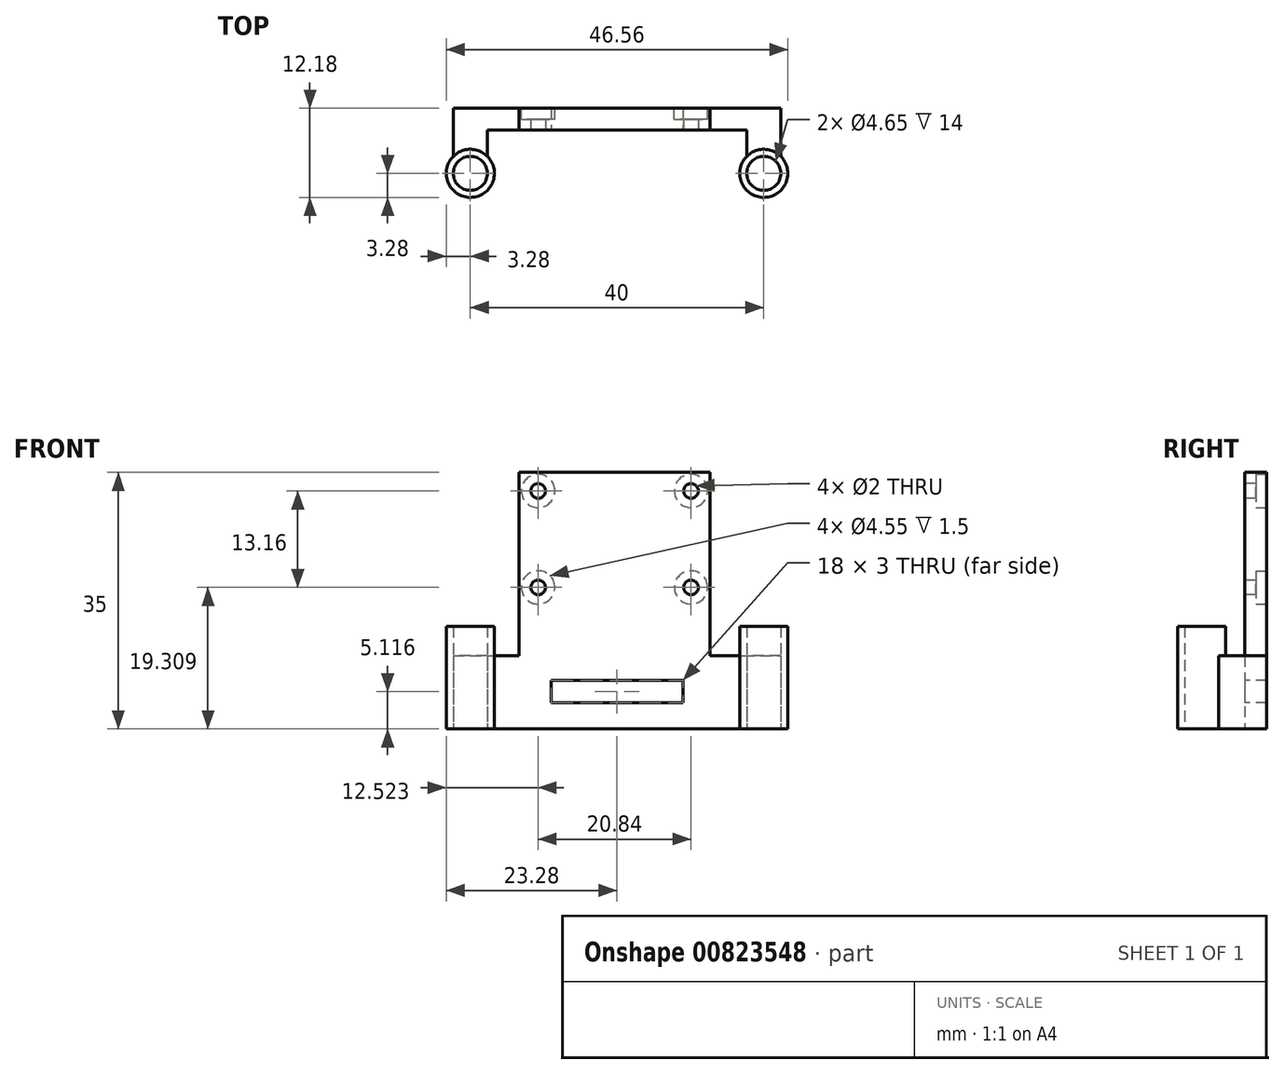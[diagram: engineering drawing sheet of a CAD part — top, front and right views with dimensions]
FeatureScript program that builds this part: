
annotation { "Feature Type Name" : "Feature", "Feature Type Description" : "" }
export const myFeature = defineFeature(function(context is Context, id is Id, definition is map)
    precondition{}
    {
        {
            var Q0;
            Q0=qCreatedBy(makeId("Top.planeOp"),FACE);
            var sketch = newSketch(context, id + "F0", { "sketchPlane" : qUnion([Q0])});
            skCircle(sketch, "E0", {"center": v(-19.76, 0) * mm, "radius": 2.33 * mm});
            skCircle(sketch, "E1", {"center": v(20.24, 0) * mm, "radius": 2.33 * mm});
            skCircle(sketch, "E2", {"center": v(-19.76, 0) * mm, "radius": 3.28 * mm});
            skCircle(sketch, "E3", {"center": v(20.24, 0) * mm, "radius": 3.28 * mm});
            skLineSegment(sketch, "E4", {"start": v(-22.08, 0) * mm, "end": v(-22.08, 8.9) * mm});
            skLineSegment(sketch, "E5", {"start": v(22.57, 0) * mm, "end": v(22.57, 8.9) * mm});
            skLineSegment(sketch, "E6", {"start": v(-19.76, 0) * mm, "end": v(20.24, 0) * mm});
            skLineSegment(sketch, "E7", {"start": v(-22.08, 8.9) * mm, "end": v(22.57, 8.9) * mm});
            skLineSegment(sketch, "E8", {"start": v(-17.43, 0) * mm, "end": v(-17.43, 8.9) * mm});
            skLineSegment(sketch, "E9", {"start": v(17.92, 0) * mm, "end": v(17.92, 8.9) * mm});
            skLineSegment(sketch, "E10", {"start": v(-17.43, 5.9) * mm, "end": v(17.92, 5.9) * mm});
            skSolve(sketch);
        }
        {
            var Q0;
            {var subQ0=sQuery(id+"F0.wireOp",EDGE,"E5");var subQ1=sQuery(id+"F0.wireOp",EDGE,"E1");var subQ2=makeQuery(id+"F0.imprint","INTERSECT",VERTEX,{"derivedFrom":[subQ1,subQ0]});Q0=makeQuery(id+"F0.imprint","IMPRINT",FACE,{"disambiguationData":[TD([[makeQuery(id+"F0.imprint","IMPRINT",EDGE,{"disambiguationData":[TD([[subQ2,1.0]])],"derivedFrom":subQ1}),-1.0]])]});}
            var Q1;
            {var subQ0=sQuery(id+"F0.wireOp",EDGE,"pIkjSwQs-KMYw-8EDy-75vt-u513Ge878Lcs");var subQ1=sQuery(id+"F0.wireOp",EDGE,"E1");var subQ2=makeQuery(id+"F0.imprint","INTERSECT",VERTEX,{"derivedFrom":[subQ1,subQ0]});Q1=makeQuery(id+"F0.imprint","IMPRINT",FACE,{"disambiguationData":[TD([[makeQuery(id+"F0.imprint","IMPRINT",EDGE,{"disambiguationData":[TD([[subQ2,1.0]])],"derivedFrom":subQ1}),-1.0]])]});}
            var Q2;
            {var subQ0=sQuery(id+"F0.wireOp",EDGE,"pIkjSwQs-KMYw-8EDy-75vt-u513Ge878Lcs");var subQ1=sQuery(id+"F0.wireOp",EDGE,"E1");var subQ2=makeQuery(id+"F0.imprint","INTERSECT",VERTEX,{"derivedFrom":[subQ1,subQ0]});Q2=makeQuery(id+"F0.imprint","IMPRINT",FACE,{"disambiguationData":[TD([[makeQuery(id+"F0.imprint","IMPRINT",EDGE,{"disambiguationData":[TD([[subQ2,-1.0]])],"derivedFrom":subQ1}),-1.0]])]});}
            var Q3;
            {var subQ0=sQuery(id+"F0.wireOp",EDGE,"PAsIG5vc-tbBl-nQOd-2SaM-8rldyLJ6n05g");Q3=makeQuery(id+"F0.imprint","IMPRINT",FACE,{"disambiguationData":[TD([[makeQuery(id+"F0.imprint","IMPRINT",EDGE,{"derivedFrom":subQ0}),1.0]])]});}
            var Q4;
            {var subQ0=sQuery(id+"F0.wireOp",EDGE,"z06Rm72J-lbv2-eatK-js9Q-tS6ydxI5LmMU.bottom");Q4=makeQuery(id+"F0.imprint","IMPRINT",FACE,{"disambiguationData":[TD([[makeQuery(id+"F0.imprint","IMPRINT",EDGE,{"derivedFrom":subQ0}),-1.0]])]});}
            var Q5;
            {var subQ0=sQuery(id+"F0.wireOp",EDGE,"zEkp0kuG-he4V-8IWa-PuKW-0BacrWcyJJLC");Q5=makeQuery(id+"F0.imprint","IMPRINT",FACE,{"disambiguationData":[TD([[makeQuery(id+"F0.imprint","IMPRINT",EDGE,{"derivedFrom":subQ0}),-1.0]])]});}
            var Q6;
            {var subQ0=sQuery(id+"F0.wireOp",EDGE,"E4");var subQ1=sQuery(id+"F0.wireOp",EDGE,"E0");var subQ2=makeQuery(id+"F0.imprint","INTERSECT",VERTEX,{"derivedFrom":[subQ1,subQ0]});Q6=makeQuery(id+"F0.imprint","IMPRINT",FACE,{"disambiguationData":[TD([[makeQuery(id+"F0.imprint","IMPRINT",EDGE,{"disambiguationData":[TD([[subQ2,1.0]])],"derivedFrom":subQ1}),-1.0]])]});}
            var Q7;
            {var subQ0=sQuery(id+"F0.wireOp",EDGE,"qbSQwhjJ-SbTz-RbyT-yrnF-y7RLgv9yjtzQ");var subQ1=sQuery(id+"F0.wireOp",EDGE,"E0");var subQ2=makeQuery(id+"F0.imprint","INTERSECT",VERTEX,{"derivedFrom":[subQ1,subQ0]});Q7=makeQuery(id+"F0.imprint","IMPRINT",FACE,{"disambiguationData":[TD([[makeQuery(id+"F0.imprint","IMPRINT",EDGE,{"disambiguationData":[TD([[subQ2,1.0]])],"derivedFrom":subQ1}),-1.0]])]});}
            var Q8;
            {var subQ0=sQuery(id+"F0.wireOp",EDGE,"E4");var subQ1=sQuery(id+"F0.wireOp",EDGE,"E0");var subQ2=makeQuery(id+"F0.imprint","INTERSECT",VERTEX,{"derivedFrom":[subQ1,subQ0]});Q8=makeQuery(id+"F0.imprint","IMPRINT",FACE,{"disambiguationData":[TD([[makeQuery(id+"F0.imprint","IMPRINT",EDGE,{"disambiguationData":[TD([[subQ2,-1.0]])],"derivedFrom":subQ1}),-1.0]])]});}
            var Q9;
            {var subQ0=sQuery(id+"F0.wireOp",EDGE,"E6");var subQ1=sQuery(id+"F0.wireOp",EDGE,"E2");var subQ2=makeQuery(id+"F0.imprint","INTERSECT",VERTEX,{"derivedFrom":[subQ1,subQ0]});Q9=makeQuery(id+"F0.imprint","IMPRINT",FACE,{"disambiguationData":[TD([[makeQuery(id+"F0.imprint","IMPRINT",EDGE,{"disambiguationData":[TD([[subQ2,-1.0]])],"derivedFrom":subQ1}),1.0]])]});}
            var Q10;
            {var subQ1=sQuery(id+"F0.wireOp",EDGE,"E4");var subQ6=sQuery(id+"F0.wireOp",EDGE,"E2");var subQ8=makeQuery(id+"F0.imprint","INTERSECT",VERTEX,{"derivedFrom":[subQ6,subQ1]});Q10=makeQuery(id+"F0.imprint","IMPRINT",FACE,{"disambiguationData":[TD([[makeQuery(id+"F0.imprint","IMPRINT",EDGE,{"disambiguationData":[TD([[subQ8,1.0]])],"derivedFrom":subQ6}),-1.0]])]});}
            var Q11;
            {var subQ5=sQuery(id+"F0.wireOp",EDGE,"E10");Q11=makeQuery(id+"F0.imprint","IMPRINT",FACE,{"disambiguationData":[TD([[makeQuery(id+"F0.imprint","IMPRINT",EDGE,{"derivedFrom":subQ5}),1.0]])]});}
            var Q12;
            {var subQ2=sQuery(id+"F0.wireOp",EDGE,"E3");var subQ5=sQuery(id+"F0.wireOp",EDGE,"E5");var subQ7=makeQuery(id+"F0.imprint","INTERSECT",VERTEX,{"derivedFrom":[subQ2,subQ5]});Q12=makeQuery(id+"F0.imprint","IMPRINT",FACE,{"disambiguationData":[TD([[makeQuery(id+"F0.imprint","IMPRINT",EDGE,{"disambiguationData":[TD([[subQ7,-1.0]])],"derivedFrom":subQ2}),-1.0]])]});}
            var Q13;
            {var subQ0=sQuery(id+"F0.wireOp",EDGE,"E6");var subQ1=sQuery(id+"F0.wireOp",EDGE,"E3");var subQ2=makeQuery(id+"F0.imprint","INTERSECT",VERTEX,{"derivedFrom":[subQ1,subQ0]});Q13=makeQuery(id+"F0.imprint","IMPRINT",FACE,{"disambiguationData":[TD([[makeQuery(id+"F0.imprint","IMPRINT",EDGE,{"disambiguationData":[TD([[subQ2,1.0]])],"derivedFrom":subQ1}),1.0]])]});}
            extrude(context, id + "F1", {"entities" : qUnion([Q0, Q1, Q2, Q3, Q4, Q5, Q6, Q7, Q8, Q9, Q10, Q11, Q12, Q13]), "depth" : 10 * mm, "offsetDistance" : 25 * mm});
        }
        {
            var Q0;
            Q0=makeQuery(id+"F1.opExtrude","CAP_FACE",FACE,{"disambiguationData":[OSD([sQuery(id+"F0.wireOp",EDGE,"E0"),sQuery(id+"F0.wireOp",EDGE,"E1"),sQuery(id+"F0.wireOp",EDGE,"E2"),sQuery(id+"F0.wireOp",EDGE,"E3"),sQuery(id+"F0.wireOp",EDGE,"E4"),sQuery(id+"F0.wireOp",EDGE,"qbSQwhjJ-SbTz-RbyT-yrnF-y7RLgv9yjtzQ"),sQuery(id+"F0.wireOp",EDGE,"zEkp0kuG-he4V-8IWa-PuKW-0BacrWcyJJLC"),sQuery(id+"F0.wireOp",EDGE,"pIkjSwQs-KMYw-8EDy-75vt-u513Ge878Lcs"),sQuery(id+"F0.wireOp",EDGE,"E5"),sQuery(id+"F0.wireOp",EDGE,"PAsIG5vc-tbBl-nQOd-2SaM-8rldyLJ6n05g"),sQuery(id+"F0.wireOp",EDGE,"z06Rm72J-lbv2-eatK-js9Q-tS6ydxI5LmMU.bottom"),sQuery(id+"F0.wireOp",EDGE,"z06Rm72J-lbv2-eatK-js9Q-tS6ydxI5LmMU.top")])],"isStart":false});
            var sketch = newSketch(context, id + "F2", { "sketchPlane" : qUnion([Q0])});
            skPoint(sketch, "E11", {"position": v(0, 12.63) * mm});
            skPoint(sketch, "E12", {"position": v(-0.1, 7.4) * mm});
            skLineSegment(sketch, "E13.bottom", {"start": v(-13.1, 5.9) * mm, "end": v(12.9, 5.9) * mm});
            skLineSegment(sketch, "E13.top", {"start": v(-13.1, 8.9) * mm, "end": v(12.9, 8.9) * mm});
            skLineSegment(sketch, "E13.left", {"start": v(-13.1, 5.9) * mm, "end": v(-13.1, 8.9) * mm});
            skLineSegment(sketch, "E13.right", {"start": v(12.9, 5.9) * mm, "end": v(12.9, 8.9) * mm});
            skSolve(sketch);
        }
        {
            var Q0;
            Q0=makeQuery(id+"F2.imprint","IMPRINT",FACE,{"disambiguationData":[TD([[makeQuery(id+"F2.imprint","IMPRINT",EDGE,{"derivedFrom":sQuery(id+"F2.wireOp",EDGE,"E13.bottom")}),1.0]])]});
            extrude(context, id + "F3", {"entities" : qUnion([Q0]), "operationType" : NewBodyOperationType.ADD, "depth" : 28 * mm, "offsetDistance" : 25 * mm});
        }
        {
            var Q0;
            Q0=makeQuery(id+"F3.boolean.opBoolean","MERGE",FACE,{"derivedFrom":[makeQuery(id+"F1.opExtrude","SWEPT_FACE",FACE,{"disambiguationData":[OSD([sQuery(id+"F0.wireOp",EDGE,"z06Rm72J-lbv2-eatK-js9Q-tS6ydxI5LmMU.top")])]}),makeQuery(id+"F3.opExtrude","SWEPT_FACE",FACE,{"disambiguationData":[OSD([sQuery(id+"F2.wireOp",EDGE,"E13.bottom")])]})]});
            var sketch = newSketch(context, id + "F4", { "sketchPlane" : qUnion([Q0])});
            skCircle(sketch, "E14", {"center": v(-10.52, 35.47) * mm, "radius": 1 * mm});
            skCircle(sketch, "E15", {"center": v(-10.52, 22.3) * mm, "radius": 1 * mm});
            skCircle(sketch, "E16", {"center": v(10.32, 35.47) * mm, "radius": 1 * mm});
            skCircle(sketch, "E17", {"center": v(10.32, 22.3) * mm, "radius": 1 * mm});
            skPoint(sketch, "E18.middle", {"position": v(0, 7.75) * mm});
            skSolve(sketch);
        }
        {
            var Q0;
            Q0=makeQuery(id+"F4.imprint","IMPRINT",FACE,{"disambiguationData":[TD([[makeQuery(id+"F4.imprint","IMPRINT",EDGE,{"derivedFrom":sQuery(id+"F4.wireOp",EDGE,"E14")}),1.0]])]});
            var Q1;
            Q1=makeQuery(id+"F4.imprint","IMPRINT",FACE,{"disambiguationData":[TD([[makeQuery(id+"F4.imprint","IMPRINT",EDGE,{"derivedFrom":sQuery(id+"F4.wireOp",EDGE,"E15")}),1.0]])]});
            var Q2;
            Q2=makeQuery(id+"F4.imprint","IMPRINT",FACE,{"disambiguationData":[TD([[makeQuery(id+"F4.imprint","IMPRINT",EDGE,{"derivedFrom":sQuery(id+"F4.wireOp",EDGE,"E17")}),1.0]])]});
            var Q3;
            Q3=makeQuery(id+"F4.imprint","IMPRINT",FACE,{"disambiguationData":[TD([[makeQuery(id+"F4.imprint","IMPRINT",EDGE,{"derivedFrom":sQuery(id+"F4.wireOp",EDGE,"E16")}),1.0]])]});
            var Q4;
            Q4=makeQuery(id+"F4.imprint","IMPRINT",FACE,{"disambiguationData":[TD([[makeQuery(id+"F4.imprint","IMPRINT",EDGE,{"derivedFrom":sQuery(id+"F4.wireOp",EDGE,"E18.bottom")}),-1.0]])]});
            extrude(context, id + "F5", {"entities" : qUnion([Q0, Q1, Q2, Q3, Q4]), "operationType" : NewBodyOperationType.REMOVE, "endBound" : BoundingType.UP_TO_NEXT, "oppositeDirection" : true, "depth" : 25 * mm, "offsetDistance" : 25 * mm});
        }
        {
            var Q0;
            Q0=makeQuery(id+"F3.boolean.opBoolean","MERGE",FACE,{"derivedFrom":[makeQuery(id+"F1.opExtrude","SWEPT_FACE",FACE,{"disambiguationData":[OSD([sQuery(id+"F0.wireOp",EDGE,"zEkp0kuG-he4V-8IWa-PuKW-0BacrWcyJJLC"),sQuery(id+"F0.wireOp",EDGE,"z06Rm72J-lbv2-eatK-js9Q-tS6ydxI5LmMU.bottom")])]}),makeQuery(id+"F3.opExtrude","SWEPT_FACE",FACE,{"disambiguationData":[OSD([sQuery(id+"F2.wireOp",EDGE,"E13.top")])]})]});
            var sketch = newSketch(context, id + "F6", { "sketchPlane" : qUnion([Q0])});
            skCircle(sketch, "E19", {"center": v(-10.32, 35.47) * mm, "radius": 2.27 * mm});
            skCircle(sketch, "E20", {"center": v(10.52, 35.47) * mm, "radius": 2.27 * mm});
            skCircle(sketch, "E21", {"center": v(-10.32, 22.3) * mm, "radius": 2.27 * mm});
            skCircle(sketch, "E22", {"center": v(10.52, 22.3) * mm, "radius": 2.27 * mm});
            skSolve(sketch);
        }
        {
            var Q0;
            Q0=makeQuery(id+"F6.imprint","IMPRINT",FACE,{"disambiguationData":[TD([[makeQuery(id+"F6.imprint","IMPRINT",EDGE,{"derivedFrom":sQuery(id+"F6.wireOp",EDGE,"E19")}),1.0]])]});
            var Q1;
            Q1=makeQuery(id+"F6.imprint","IMPRINT",FACE,{"disambiguationData":[TD([[makeQuery(id+"F6.imprint","IMPRINT",EDGE,{"derivedFrom":sQuery(id+"F6.wireOp",EDGE,"E21")}),1.0]])]});
            var Q2;
            Q2=makeQuery(id+"F6.imprint","IMPRINT",FACE,{"disambiguationData":[TD([[makeQuery(id+"F6.imprint","IMPRINT",EDGE,{"derivedFrom":sQuery(id+"F6.wireOp",EDGE,"E22")}),1.0]])]});
            var Q3;
            Q3=makeQuery(id+"F6.imprint","IMPRINT",FACE,{"disambiguationData":[TD([[makeQuery(id+"F6.imprint","IMPRINT",EDGE,{"derivedFrom":sQuery(id+"F6.wireOp",EDGE,"E20")}),1.0]])]});
            extrude(context, id + "F7", {"entities" : qUnion([Q0, Q1, Q2, Q3]), "operationType" : NewBodyOperationType.REMOVE, "oppositeDirection" : true, "depth" : 1.5 * mm, "offsetDistance" : 25 * mm});
        }
        {
            var Q0;
            Q0=makeQuery(id+"F1.opExtrude","CAP_FACE",FACE,{"disambiguationData":[OSD([sQuery(id+"F0.wireOp",EDGE,"E0"),sQuery(id+"F0.wireOp",EDGE,"E1"),sQuery(id+"F0.wireOp",EDGE,"E2"),sQuery(id+"F0.wireOp",EDGE,"E3"),sQuery(id+"F0.wireOp",EDGE,"E4"),sQuery(id+"F0.wireOp",EDGE,"E5"),sQuery(id+"F0.wireOp",EDGE,"E7"),sQuery(id+"F0.wireOp",EDGE,"E8"),sQuery(id+"F0.wireOp",EDGE,"E9"),sQuery(id+"F0.wireOp",EDGE,"E10")])],"isStart":true});
            extrude(context, id + "F8", {"entities" : qUnion([Q0]), "operationType" : NewBodyOperationType.REMOVE, "oppositeDirection" : true, "depth" : 3 * mm, "offsetDistance" : 25 * mm});
        }
        {
            var Q0;
            {var subQ0=sQuery(id+"F0.wireOp",EDGE,"E5");var subQ1=sQuery(id+"F0.wireOp",EDGE,"E3");var subQ2=sQuery(id+"F0.wireOp",EDGE,"E7");var subQ3=sQuery(id+"F0.wireOp",EDGE,"E1");var subQ4=sQuery(id+"F0.wireOp",EDGE,"E9");var subQ5=sQuery(id+"F0.wireOp",EDGE,"E10");Q0=makeQuery(id+"F3.boolean.opBoolean","SPLIT",FACE,{"disambiguationData":[TD([makeQuery(id+"F1.opExtrude","SWEPT_FACE",FACE,{"disambiguationData":[OSD([subQ3])]})])],"derivedFrom":makeQuery(id+"F1.opExtrude","CAP_FACE",FACE,{"disambiguationData":[OSD([sQuery(id+"F0.wireOp",EDGE,"E0"),subQ3,sQuery(id+"F0.wireOp",EDGE,"E2"),subQ1,sQuery(id+"F0.wireOp",EDGE,"E4"),subQ0,subQ2,sQuery(id+"F0.wireOp",EDGE,"E8"),subQ4,subQ5])],"isStart":false})});}
            var Q1;
            {var subQ0=sQuery(id+"F0.wireOp",EDGE,"E7");var subQ1=sQuery(id+"F0.wireOp",EDGE,"E4");var subQ2=sQuery(id+"F0.wireOp",EDGE,"E2");var subQ3=sQuery(id+"F0.wireOp",EDGE,"E0");var subQ4=sQuery(id+"F0.wireOp",EDGE,"E10");var subQ5=sQuery(id+"F0.wireOp",EDGE,"E8");Q1=makeQuery(id+"F3.boolean.opBoolean","SPLIT",FACE,{"disambiguationData":[TD([makeQuery(id+"F1.opExtrude","SWEPT_FACE",FACE,{"disambiguationData":[OSD([subQ3])]})])],"derivedFrom":makeQuery(id+"F1.opExtrude","CAP_FACE",FACE,{"disambiguationData":[OSD([subQ3,sQuery(id+"F0.wireOp",EDGE,"E1"),subQ2,sQuery(id+"F0.wireOp",EDGE,"E3"),subQ1,sQuery(id+"F0.wireOp",EDGE,"E5"),subQ0,subQ5,sQuery(id+"F0.wireOp",EDGE,"E9"),subQ4])],"isStart":false})});}
            extrude(context, id + "F9", {"entities" : qUnion([Q0, Q1]), "operationType" : NewBodyOperationType.ADD, "depth" : 3 * mm, "offsetDistance" : 25 * mm});
        }
        {
            var Q0;
            {var subQ0=sQuery(id+"F0.wireOp",EDGE,"E5");var subQ1=sQuery(id+"F0.wireOp",EDGE,"E3");var subQ2=sQuery(id+"F0.wireOp",EDGE,"E7");var subQ3=sQuery(id+"F0.wireOp",EDGE,"E1");var subQ4=sQuery(id+"F0.wireOp",EDGE,"E9");var subQ5=sQuery(id+"F0.wireOp",EDGE,"E10");var subQ6=sQuery(id+"F0.wireOp",EDGE,"E8");var subQ7=sQuery(id+"F0.wireOp",EDGE,"E4");var subQ8=sQuery(id+"F0.wireOp",EDGE,"E2");var subQ9=sQuery(id+"F0.wireOp",EDGE,"E0");Q0=makeQuery(id+"F9.opExtrude","CAP_FACE",FACE,{"disambiguationData":[OSD([subQ9,subQ3,subQ8,subQ1,subQ7,subQ0,subQ2,subQ6,subQ4,subQ5]),TDD([makeQuery(id+"F3.boolean.opBoolean","SPLIT",FACE,{"disambiguationData":[TD([makeQuery(id+"F1.opExtrude","SWEPT_FACE",FACE,{"disambiguationData":[OSD([subQ3])]})])],"derivedFrom":makeQuery(id+"F1.opExtrude","CAP_FACE",FACE,{"disambiguationData":[OSD([subQ9,subQ3,subQ8,subQ1,subQ7,subQ0,subQ2,subQ6,subQ4,subQ5])],"isStart":false})})])],"isStart":false});}
            var sketch = newSketch(context, id + "F10", { "sketchPlane" : qUnion([Q0])});
            skCircle(sketch, "E23", {"center": v(20.24, 0) * mm, "radius": 2.33 * mm});
            skCircle(sketch, "E24", {"center": v(20.24, 0) * mm, "radius": 3.28 * mm});
            skSolve(sketch);
        }
        {
            var Q0;
            {var subQ0=sQuery(id+"F0.wireOp",EDGE,"E7");var subQ1=sQuery(id+"F0.wireOp",EDGE,"E4");var subQ2=sQuery(id+"F0.wireOp",EDGE,"E2");var subQ3=sQuery(id+"F0.wireOp",EDGE,"E0");var subQ4=sQuery(id+"F0.wireOp",EDGE,"E10");var subQ5=sQuery(id+"F0.wireOp",EDGE,"E8");var subQ6=sQuery(id+"F0.wireOp",EDGE,"E9");var subQ7=sQuery(id+"F0.wireOp",EDGE,"E5");var subQ8=sQuery(id+"F0.wireOp",EDGE,"E3");var subQ9=sQuery(id+"F0.wireOp",EDGE,"E1");Q0=makeQuery(id+"F9.opExtrude","CAP_FACE",FACE,{"disambiguationData":[OSD([subQ3,subQ9,subQ2,subQ8,subQ1,subQ7,subQ0,subQ5,subQ6,subQ4]),TDD([makeQuery(id+"F3.boolean.opBoolean","SPLIT",FACE,{"disambiguationData":[TD([makeQuery(id+"F1.opExtrude","SWEPT_FACE",FACE,{"disambiguationData":[OSD([subQ3])]})])],"derivedFrom":makeQuery(id+"F1.opExtrude","CAP_FACE",FACE,{"disambiguationData":[OSD([subQ3,subQ9,subQ2,subQ8,subQ1,subQ7,subQ0,subQ5,subQ6,subQ4])],"isStart":false})})])],"isStart":false});}
            var sketch = newSketch(context, id + "F11", { "sketchPlane" : qUnion([Q0])});
            skCircle(sketch, "E25", {"center": v(-19.76, 0) * mm, "radius": 2.33 * mm});
            skCircle(sketch, "E26", {"center": v(-19.76, 0) * mm, "radius": 3.28 * mm});
            skSolve(sketch);
        }
        {
            var Q0;
            Q0=makeQuery(id+"F10.imprint","IMPRINT",FACE,{"disambiguationData":[TD([[makeQuery(id+"F10.imprint","IMPRINT",EDGE,{"derivedFrom":sQuery(id+"F10.wireOp",EDGE,"E23")}),-1.0]])]});
            var Q1;
            Q1=makeQuery(id+"F11.imprint","IMPRINT",FACE,{"disambiguationData":[TD([[makeQuery(id+"F11.imprint","IMPRINT",EDGE,{"derivedFrom":sQuery(id+"F11.wireOp",EDGE,"E25")}),-1.0]])]});
            extrude(context, id + "F12", {"entities" : qUnion([Q0, Q1]), "operationType" : NewBodyOperationType.ADD, "depth" : 4 * mm, "offsetDistance" : 25 * mm});
        }
        {
            var Q0;
            {var subQ0=makeQuery(id+"F3.opExtrude","SWEPT_FACE",FACE,{"disambiguationData":[OSD([sQuery(id+"F2.wireOp",EDGE,"E13.bottom")])]});var subQ1=sQuery(id+"F0.wireOp",EDGE,"E10");var subQ2=makeQuery(id+"F1.opExtrude","SWEPT_FACE",FACE,{"disambiguationData":[OSD([subQ1])]});var subQ3=sQuery(id+"F0.wireOp",EDGE,"E9");var subQ4=sQuery(id+"F0.wireOp",EDGE,"E8");var subQ6=makeQuery(id+"F1.opExtrude","CAP_EDGE",EDGE,{"disambiguationData":[OSD([subQ1])],"isStart":false});Q0=makeQuery(id+"F9.boolean.opBoolean","MERGE",FACE,{"derivedFrom":[makeQuery(id+"F3.boolean.opBoolean","MERGE",FACE,{"derivedFrom":[subQ2,subQ0]}),makeQuery(id+"F9.opExtrude","SWEPT_FACE",FACE,{"disambiguationData":[OSD([subQ1]),TDD([makeQuery(id+"F3.boolean.opBoolean","SPLIT",EDGE,{"disambiguationData":[TD([makeQuery(id+"F1.opExtrude","SWEPT_FACE",FACE,{"disambiguationData":[OSD([subQ4])]})])],"derivedFrom":subQ6})])]}),makeQuery(id+"F9.opExtrude","SWEPT_FACE",FACE,{"disambiguationData":[OSD([subQ1]),TDD([makeQuery(id+"F3.boolean.opBoolean","SPLIT",EDGE,{"disambiguationData":[TD([makeQuery(id+"F1.opExtrude","SWEPT_FACE",FACE,{"disambiguationData":[OSD([subQ3])]})])],"derivedFrom":subQ6})])]})]});}
            var sketch = newSketch(context, id + "F13", { "sketchPlane" : qUnion([Q0])});
            skLineSegment(sketch, "E27.bottom", {"start": v(-8.76, 9.62) * mm, "end": v(9.24, 9.62) * mm});
            skLineSegment(sketch, "E27.top", {"start": v(-8.76, 6.62) * mm, "end": v(9.24, 6.62) * mm});
            skLineSegment(sketch, "E27.left", {"start": v(-8.76, 9.62) * mm, "end": v(-8.76, 6.62) * mm});
            skLineSegment(sketch, "E27.right", {"start": v(9.24, 9.62) * mm, "end": v(9.24, 6.62) * mm});
            skLineSegment(sketch, "E28", {"start": v(0.24, 3) * mm, "end": v(0.24, 6.62) * mm});
            skSolve(sketch);
        }
        {
            var Q0;
            Q0=makeQuery(id+"F13.imprint","IMPRINT",FACE,{"disambiguationData":[TD([[makeQuery(id+"F13.imprint","IMPRINT",EDGE,{"derivedFrom":sQuery(id+"F13.wireOp",EDGE,"E27.bottom")}),-1.0]])]});
            extrude(context, id + "F14", {"entities" : qUnion([Q0]), "operationType" : NewBodyOperationType.REMOVE, "endBound" : BoundingType.THROUGH_ALL, "oppositeDirection" : true, "depth" : 25 * mm, "offsetDistance" : 25 * mm});
        }
    });
